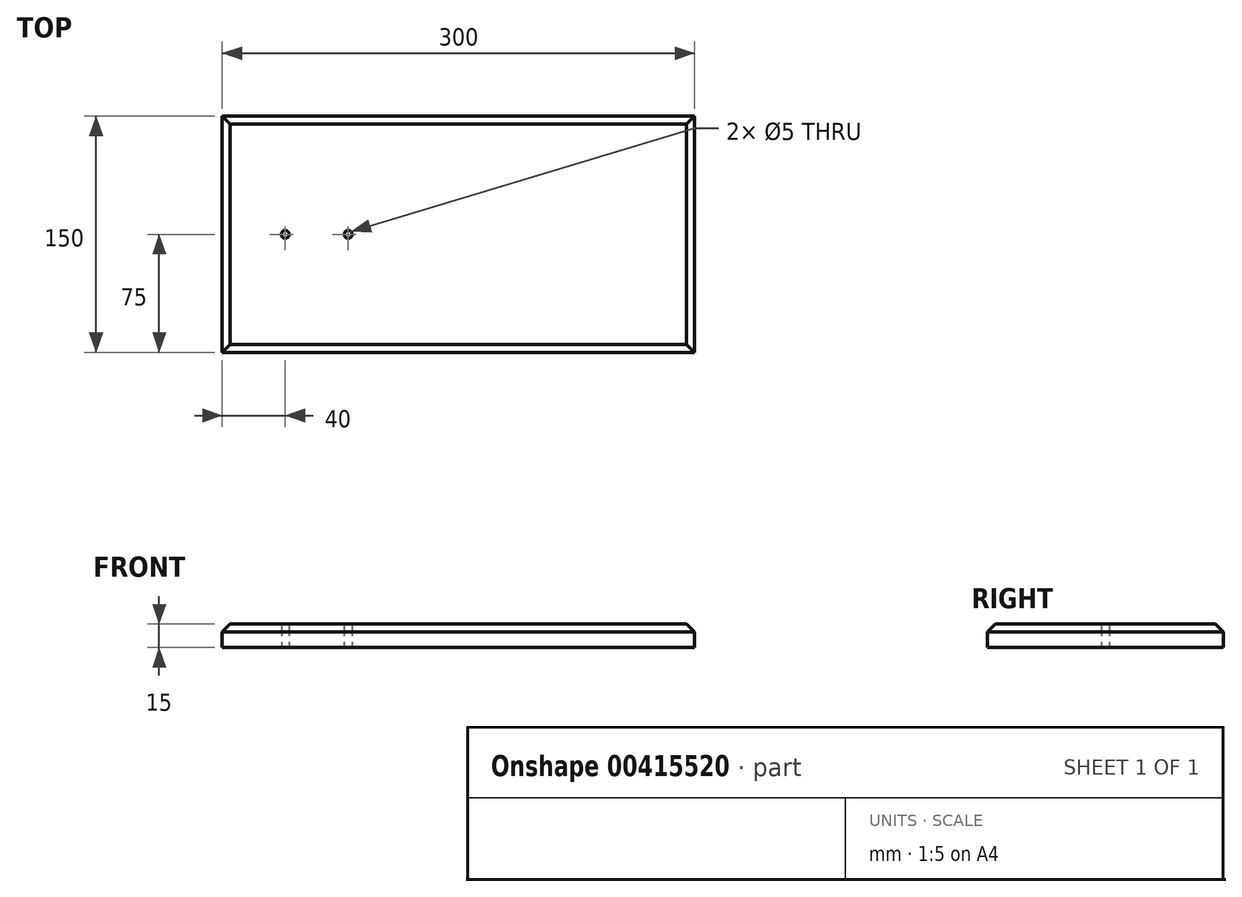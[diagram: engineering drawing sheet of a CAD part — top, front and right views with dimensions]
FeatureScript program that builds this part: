
annotation { "Feature Type Name" : "Feature", "Feature Type Description" : "" }
export const myFeature = defineFeature(function(context is Context, id is Id, definition is map)
    precondition{}
    {
        {
            var Q0;
            Q0=qCreatedBy(makeId("Top.planeOp"),FACE);
            var sketch = newSketch(context, id + "F0", { "sketchPlane" : qUnion([Q0])});
            skLineSegment(sketch, "E0.bottom", {"start": v(0, 0) * mm, "end": v(300, 0) * mm});
            skLineSegment(sketch, "E0.top", {"start": v(0, 150) * mm, "end": v(300, 150) * mm});
            skLineSegment(sketch, "E0.left", {"start": v(0, 0) * mm, "end": v(0, 150) * mm});
            skLineSegment(sketch, "E0.right", {"start": v(300, 0) * mm, "end": v(300, 150) * mm});
            skSolve(sketch);
        }
        {
            var Q0;
            Q0=makeQuery(id+"F0.imprint","IMPRINT",FACE,{"disambiguationData":[TD([[makeQuery(id+"F0.imprint","IMPRINT",EDGE,{"derivedFrom":sQuery(id+"F0.wireOp",EDGE,"E0.bottom")}),1.0]])]});
            extrude(context, id + "F1", {"entities" : qUnion([Q0]), "depth" : 15 * mm});
        }
        {
            var Q0;
            Q0=makeQuery(id+"F1.opExtrude","CAP_EDGE",EDGE,{"disambiguationData":[OSD([sQuery(id+"F0.wireOp",EDGE,"E0.bottom")])],"isStart":false});
            var Q1;
            Q1=makeQuery(id+"F1.opExtrude","CAP_EDGE",EDGE,{"disambiguationData":[OSD([sQuery(id+"F0.wireOp",EDGE,"E0.right")])],"isStart":false});
            var Q2;
            Q2=makeQuery(id+"F1.opExtrude","CAP_EDGE",EDGE,{"disambiguationData":[OSD([sQuery(id+"F0.wireOp",EDGE,"E0.top")])],"isStart":false});
            var Q3;
            Q3=makeQuery(id+"F1.opExtrude","CAP_EDGE",EDGE,{"disambiguationData":[OSD([sQuery(id+"F0.wireOp",EDGE,"E0.left")])],"isStart":false});
            chamfer(context, id + "F2", {"entities" : qUnion([Q0, Q1, Q2, Q3]), "width" : 5.08 * mm, "tangentPropagation" : true});
        }
        {
            var Q0;
            Q0=makeQuery(id+"F1.opExtrude","CAP_FACE",FACE,{"disambiguationData":[OSD([sQuery(id+"F0.wireOp",EDGE,"E0.bottom"),sQuery(id+"F0.wireOp",EDGE,"E0.top"),sQuery(id+"F0.wireOp",EDGE,"E0.left"),sQuery(id+"F0.wireOp",EDGE,"E0.right")])],"isStart":true});
            var sketch = newSketch(context, id + "F3", { "sketchPlane" : qUnion([Q0])});
            skLineSegment(sketch, "E1", {"start": v(80, -75) * mm, "end": v(40, -75) * mm});
            skSolve(sketch);
        }
        {
            var Q0;
            Q0=sQuery(id+"F3.wireOp",VERTEX,"E1.end");
            var Q1;
            Q1=sQuery(id+"F3.wireOp",VERTEX,"E1.start");
            var Q2;
            Q2=makeQuery(id+"F1.opExtrude","SWEPT_BODY",BODY,{"disambiguationData":[OSD([sQuery(id+"F0.wireOp",EDGE,"E0.bottom"),sQuery(id+"F0.wireOp",EDGE,"E0.top"),sQuery(id+"F0.wireOp",EDGE,"E0.left"),sQuery(id+"F0.wireOp",EDGE,"E0.right")])]});
            hole(context, id + "F4", {"style" : HoleStyle.SIMPLE, "endStyle" : HoleEndStyle.THROUGH, "holeDiameter" : 5 * mm, "isTappedThrough" : true, "tappedDepth" : 12.7 * mm, "tapClearance" : 3, "locations" : qUnion([Q0, Q1]), "scope" : qUnion([Q2])});
        }
    });
